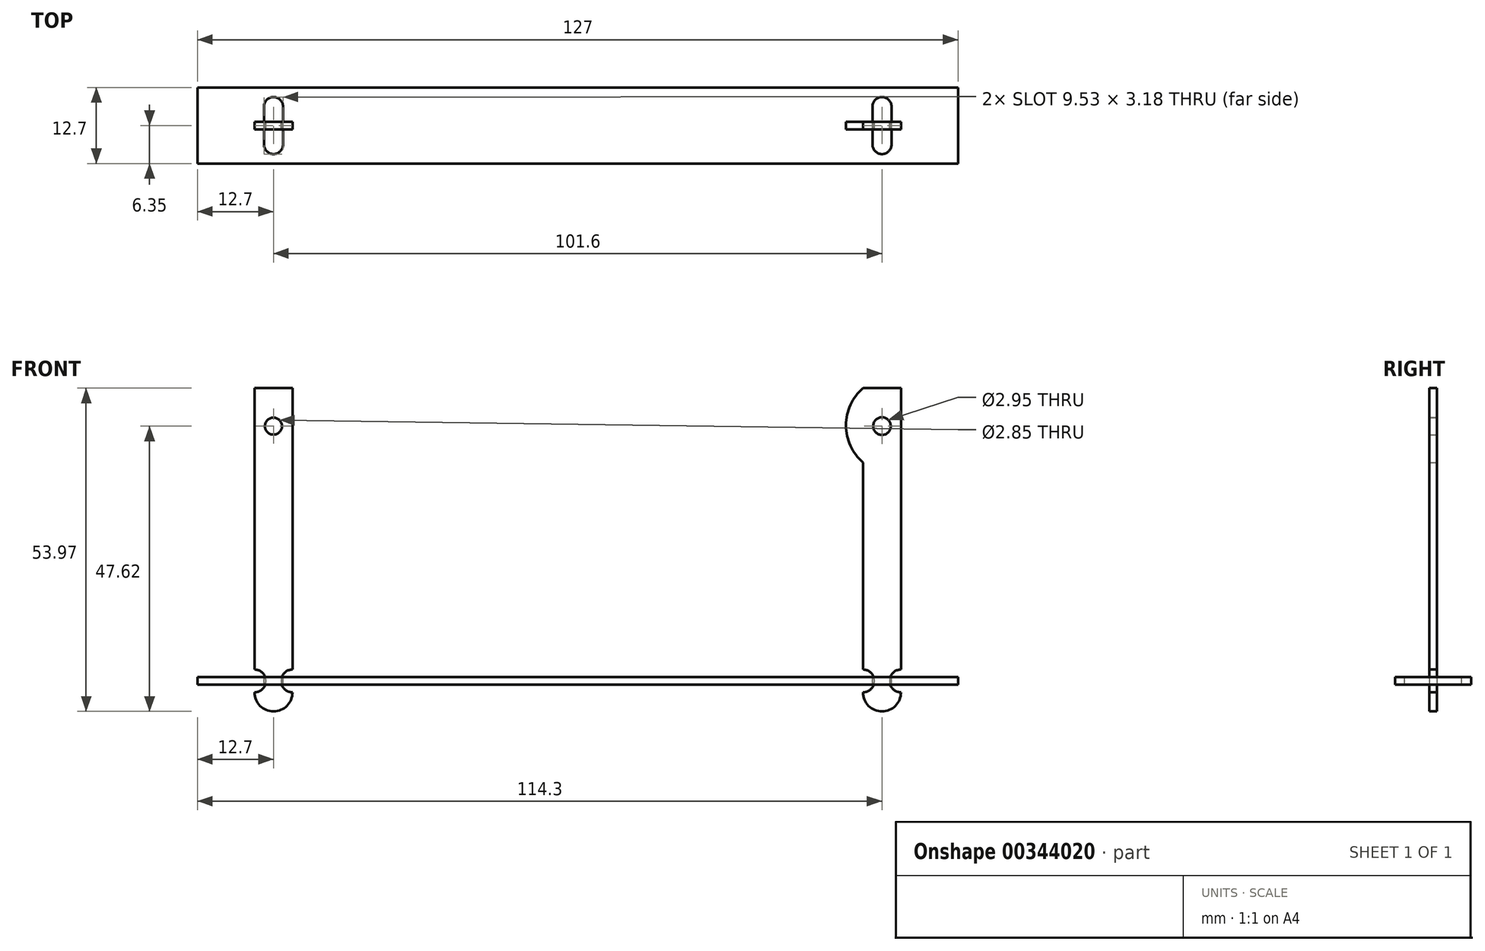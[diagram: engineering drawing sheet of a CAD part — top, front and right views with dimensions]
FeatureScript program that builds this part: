
annotation { "Feature Type Name" : "Feature", "Feature Type Description" : "" }
export const myFeature = defineFeature(function(context is Context, id is Id, definition is map)
    precondition{}
    {
        {
            var Q0;
            Q0=qCreatedBy(makeId("Front.planeOp"),FACE);
            var sketch = newSketch(context, id + "F0", { "sketchPlane" : qUnion([Q0])});
            skLineSegment(sketch, "E0.bottom", {"start": v(47.63, 0) * mm, "end": v(53.98, 0) * mm});
            skLineSegment(sketch, "E0.top", {"start": v(47.63, -50.8) * mm, "end": v(53.98, -50.8) * mm, "construction": true});
            skLineSegment(sketch, "E0.left", {"start": v(47.63, -12.42) * mm, "end": v(47.63, -47) * mm});
            skLineSegment(sketch, "E0.right", {"start": v(53.98, 0) * mm, "end": v(53.98, -46.99) * mm});
            skLineSegment(sketch, "E1.bottom", {"start": v(-53.98, 0) * mm, "end": v(-47.62, 0) * mm});
            skLineSegment(sketch, "E1.top", {"start": v(-53.98, -50.8) * mm, "end": v(-47.62, -50.8) * mm, "construction": true});
            skLineSegment(sketch, "E1.left", {"start": v(-53.98, 0) * mm, "end": v(-53.98, -47) * mm});
            skLineSegment(sketch, "E1.right", {"start": v(-47.62, 0) * mm, "end": v(-47.62, -47) * mm});
            skArc(sketch, "E2", {"start": v(-53.98, -50.8) * mm, "mid": v(-50.8, -53.98) * mm, "end": v(-47.63, -50.8) * mm});
            skCircle(sketch, "E3", {"center": v(-50.8, -6.35) * mm, "radius": 1.42 * mm});
            skPoint(sketch, "E3.centerSnap0", {"position": v(-50.8, 0) * mm});
            skArc(sketch, "E4", {"start": v(-53.98, -50.8) * mm, "mid": v(-52.07, -48.9) * mm, "end": v(-53.98, -47) * mm});
            skArc(sketch, "E5", {"start": v(47.63, -50.8) * mm, "mid": v(50.8, -53.98) * mm, "end": v(53.98, -50.8) * mm});
            skArc(sketch, "E6", {"start": v(-47.62, -47) * mm, "mid": v(-49.53, -48.9) * mm, "end": v(-47.62, -50.8) * mm});
            skArc(sketch, "E7", {"start": v(47.63, -50.8) * mm, "mid": v(49.53, -48.9) * mm, "end": v(47.63, -47) * mm});
            skArc(sketch, "E8", {"start": v(53.98, -47) * mm, "mid": v(52.07, -48.9) * mm, "end": v(53.98, -50.8) * mm});
            skPoint(sketch, "E9", {"position": v(50.8, 0) * mm});
            skCircle(sketch, "E10", {"center": v(50.8, -6.35) * mm, "radius": 1.47 * mm});
            skArc(sketch, "E11", {"start": v(47.63, 0) * mm, "mid": v(44.8, -6.2) * mm, "end": v(47.63, -12.42) * mm});
            skSolve(sketch);
        }
        {
            var Q0;
            Q0=makeQuery(id+"F0.imprint","IMPRINT",FACE,{"disambiguationData":[TD([[makeQuery(id+"F0.imprint","IMPRINT",EDGE,{"derivedFrom":sQuery(id+"F0.wireOp",EDGE,"E1.bottom")}),-1.0]])]});
            extrude(context, id + "F1", {"entities" : qUnion([Q0]), "endBound" : BoundingType.SYMMETRIC, "depth" : 1.27 * mm, "offsetDistance" : 25.4 * mm});
        }
        {
            var Q0;
            Q0=qCreatedBy(makeId("Top.planeOp"),FACE);
            var sketch = newSketch(context, id + "F2", { "sketchPlane" : qUnion([Q0])});
            skLineSegment(sketch, "E12.bottom", {"start": v(63.5, -6.35) * mm, "end": v(-63.5, -6.35) * mm});
            skLineSegment(sketch, "E12.top", {"start": v(63.5, 6.35) * mm, "end": v(-63.5, 6.35) * mm});
            skLineSegment(sketch, "E12.left", {"start": v(63.5, -6.35) * mm, "end": v(63.5, 6.35) * mm});
            skLineSegment(sketch, "E12.right", {"start": v(-63.5, -6.35) * mm, "end": v(-63.5, 6.35) * mm});
            skPoint(sketch, "E12.middle", {"position": v(0, 0) * mm});
            skLineSegment(sketch, "E13", {"start": v(-50.8, -3.18) * mm, "end": v(-50.8, 3.18) * mm});
            skArc(sketch, "E14.0.startCap", {"start": v(-49.21, -3.18) * mm, "mid": v(-50.8, -4.76) * mm, "end": v(-52.39, -3.17) * mm});
            skArc(sketch, "E14.0.endCap", {"start": v(-52.39, 3.18) * mm, "mid": v(-50.8, 4.76) * mm, "end": v(-49.21, 3.17) * mm});
            skLineSegment(sketch, "E14.0.left", {"start": v(-52.39, -3.18) * mm, "end": v(-52.39, 3.17) * mm});
            skLineSegment(sketch, "E14.0.right", {"start": v(-49.21, -3.18) * mm, "end": v(-49.21, 3.17) * mm});
            skLineSegment(sketch, "E15", {"start": v(0, -6.35) * mm, "end": v(0, 6.35) * mm, "construction": true});
            skArc(sketch, "E16.MirrorCS", {"start": v(52.39, 3.18) * mm, "mid": v(50.8, 4.76) * mm, "end": v(49.21, 3.18) * mm});
            skArc(sketch, "E17.MirrorCS", {"start": v(49.21, -3.17) * mm, "mid": v(50.8, -4.76) * mm, "end": v(52.39, -3.17) * mm});
            skLineSegment(sketch, "E18.MirrorCS", {"start": v(52.39, -3.17) * mm, "end": v(52.39, 3.18) * mm});
            skLineSegment(sketch, "E19.MirrorCS", {"start": v(49.21, -3.17) * mm, "end": v(49.21, 3.18) * mm});
            skSolve(sketch);
        }
        {
            var Q0;
            Q0=makeQuery(id+"F2.imprint","IMPRINT",FACE,{"disambiguationData":[TD([[makeQuery(id+"F2.imprint","IMPRINT",EDGE,{"derivedFrom":sQuery(id+"F2.wireOp",EDGE,"E12.bottom")}),-1.0]])]});
            extrude(context, id + "F3", {"entities" : qUnion([Q0]), "oppositeDirection" : true, "depth" : 49.53 * mm, "offsetDistance" : 25.4 * mm, "hasSecondDirection" : true, "secondDirectionOppositeDirection" : true, "secondDirectionDepth" : 48.26 * mm});
        }
        {
            var Q0;
            Q0=makeQuery(id+"F0.imprint","IMPRINT",FACE,{"disambiguationData":[TD([[makeQuery(id+"F0.imprint","IMPRINT",EDGE,{"derivedFrom":sQuery(id+"F0.wireOp",EDGE,"E0.bottom")}),-1.0]])]});
            extrude(context, id + "F4", {"entities" : qUnion([Q0]), "endBound" : BoundingType.SYMMETRIC, "depth" : 1.27 * mm, "offsetDistance" : 25.4 * mm});
        }
    });
